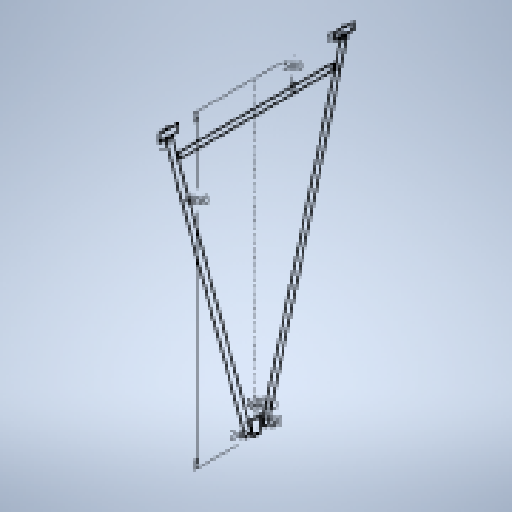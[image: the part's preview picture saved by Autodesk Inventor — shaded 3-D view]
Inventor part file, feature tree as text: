
AUTODESK INVENTOR PART (.ipt)
format: ipt  version: 2024.2 (Build 282272000, 272)  size: 148,992 bytes
history: native  units: mm
features: sketch x1
ambient origin geometry x8: Origin, YZ Plane, XZ Plane, XY Plane, X Axis, Y Axis, Z Axis, Center Point
feature tree (1):
  sketch  "Sketch2"  dims[d0=120.0mm d1=240.0mm d2=4850.0mm d3=300.0mm d4=110.0mm d5=100.0mm d6=20.0mm d7=50.0mm d8=15.0deg d9=16.0mm d10=500.0mm d11=10.0mm]
